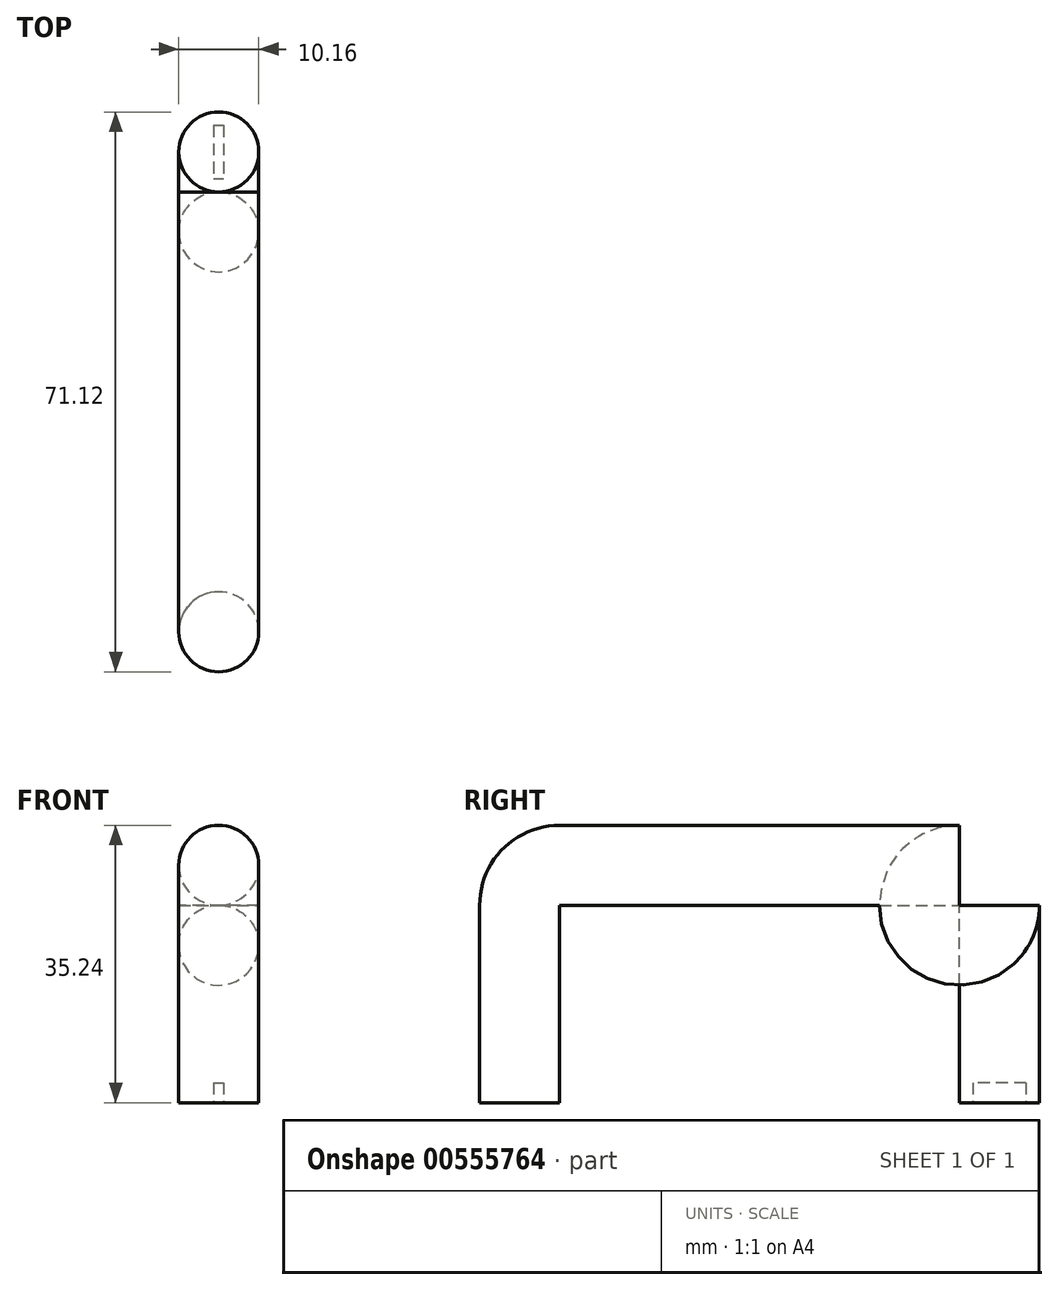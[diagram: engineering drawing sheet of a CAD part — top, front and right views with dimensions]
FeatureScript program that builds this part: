
annotation { "Feature Type Name" : "Feature", "Feature Type Description" : "" }
export const myFeature = defineFeature(function(context is Context, id is Id, definition is map)
    precondition{}
    {
        {
            var Q0;
            Q0=qCreatedBy(makeId("Front.planeOp"),FACE);
            var sketch = newSketch(context, id + "F0", { "sketchPlane" : qUnion([Q0])});
            skCircle(sketch, "E0", {"center": v(0, 0) * mm, "radius": 5.08 * mm});
            skSolve(sketch);
        }
        {
            var Q0;
            Q0=makeQuery(id+"F0.imprint","IMPRINT",FACE,{"disambiguationData":[TD([[makeQuery(id+"F0.imprint","IMPRINT",EDGE,{"derivedFrom":sQuery(id+"F0.wireOp",EDGE,"E0")}),1.0]])]});
            extrude(context, id + "F1", {"entities" : qUnion([Q0]), "depth" : 50.8 * mm, "offsetDistance" : 25.4 * mm});
        }
        {
            var Q0;
            Q0=qCreatedBy(makeId("Top.planeOp"),FACE);
            cPlane(context, id + "F2", {"entities" : qUnion([Q0]), "cplaneType" : CPlaneType.OFFSET, "offset" : 5.08 * mm, "oppositeDirection" : true, "width" : 152.4 * mm, "height" : 152.4 * mm});
        }
        {
            var Q0;
            Q0=qCreatedBy(id+"F2.planeOp",FACE);
            var sketch = newSketch(context, id + "F3", { "sketchPlane" : qUnion([Q0])});
            skCircle(sketch, "E1", {"center": v(0, -55.88) * mm, "radius": 5.08 * mm});
            skCircle(sketch, "E2", {"center": v(0, 5.08) * mm, "radius": 5.08 * mm});
            skSolve(sketch);
        }
        {
            var Q0;
            Q0=makeQuery(id+"F3.imprint","IMPRINT",FACE,{"disambiguationData":[TD([[makeQuery(id+"F3.imprint","IMPRINT",EDGE,{"derivedFrom":sQuery(id+"F3.wireOp",EDGE,"E1")}),1.0]])]});
            var Q1;
            Q1=makeQuery(id+"F3.imprint","IMPRINT",FACE,{"disambiguationData":[TD([[makeQuery(id+"F3.imprint","IMPRINT",EDGE,{"derivedFrom":sQuery(id+"F3.wireOp",EDGE,"E2")}),1.0]])]});
            extrude(context, id + "F4", {"entities" : qUnion([Q0, Q1]), "oppositeDirection" : true, "depth" : 25.08 * mm, "offsetDistance" : 25.4 * mm});
        }
        {
            var Q0;
            Q0=qCreatedBy(makeId("Right.planeOp"),FACE);
            var sketch = newSketch(context, id + "F5", { "sketchPlane" : qUnion([Q0])});
            skArc(sketch, "E3", {"start": v(-50.8, 0) * mm, "mid": v(-54.4, -1.49) * mm, "end": v(-55.88, -5.08) * mm});
            skArc(sketch, "E4", {"start": v(5.08, -5.08) * mm, "mid": v(3.6, -1.49) * mm, "end": v(0, 0) * mm});
            skSolve(sketch);
        }
        {
            var Q0;
            Q0=makeQuery(id+"F1.opExtrude","CAP_FACE",FACE,{"disambiguationData":[OSD([sQuery(id+"F0.wireOp",EDGE,"E0")])],"isStart":true});
            var Q1;
            Q1=sQuery(id+"F5.wireOp",EDGE,"E4");
            sweep(context, id + "F6", {"operationType" : NewBodyOperationType.ADD, "profiles" : qUnion([Q0]), "path" : qUnion([Q1])});
        }
        {
            var Q0;
            Q0=makeQuery(id+"F1.opExtrude","CAP_FACE",FACE,{"disambiguationData":[OSD([sQuery(id+"F0.wireOp",EDGE,"E0")])],"isStart":false});
            var Q1;
            Q1=sQuery(id+"F5.wireOp",EDGE,"E3");
            sweep(context, id + "F7", {"operationType" : NewBodyOperationType.ADD, "profiles" : qUnion([Q0]), "path" : qUnion([Q1])});
        }
        {
            var Q0;
            Q0=makeQuery(id+"F4.opExtrude","CAP_FACE",FACE,{"disambiguationData":[OSD([sQuery(id+"F3.wireOp",EDGE,"E2")])],"isStart":false});
            var sketch = newSketch(context, id + "F8", { "sketchPlane" : qUnion([Q0])});
            skLineSegment(sketch, "E5.bottom", {"start": v(-0.63, -8.45) * mm, "end": v(0.63, -8.45) * mm});
            skLineSegment(sketch, "E5.top", {"start": v(-0.63, -1.7) * mm, "end": v(0.63, -1.7) * mm});
            skLineSegment(sketch, "E5.left", {"start": v(-0.63, -8.45) * mm, "end": v(-0.63, -1.7) * mm});
            skLineSegment(sketch, "E5.right", {"start": v(0.63, -8.45) * mm, "end": v(0.63, -1.7) * mm});
            skPoint(sketch, "E5.middle", {"position": v(0, -5.08) * mm});
            skSolve(sketch);
        }
        {
            var Q0;
            Q0=makeQuery(id+"F8.imprint","IMPRINT",FACE,{"disambiguationData":[TD([[makeQuery(id+"F8.imprint","IMPRINT",EDGE,{"derivedFrom":sQuery(id+"F8.wireOp",EDGE,"E5.bottom")}),1.0]])]});
            extrude(context, id + "F9", {"entities" : qUnion([Q0]), "operationType" : NewBodyOperationType.REMOVE, "oppositeDirection" : true, "depth" : 2.54 * mm, "offsetDistance" : 25.4 * mm});
        }
    });
